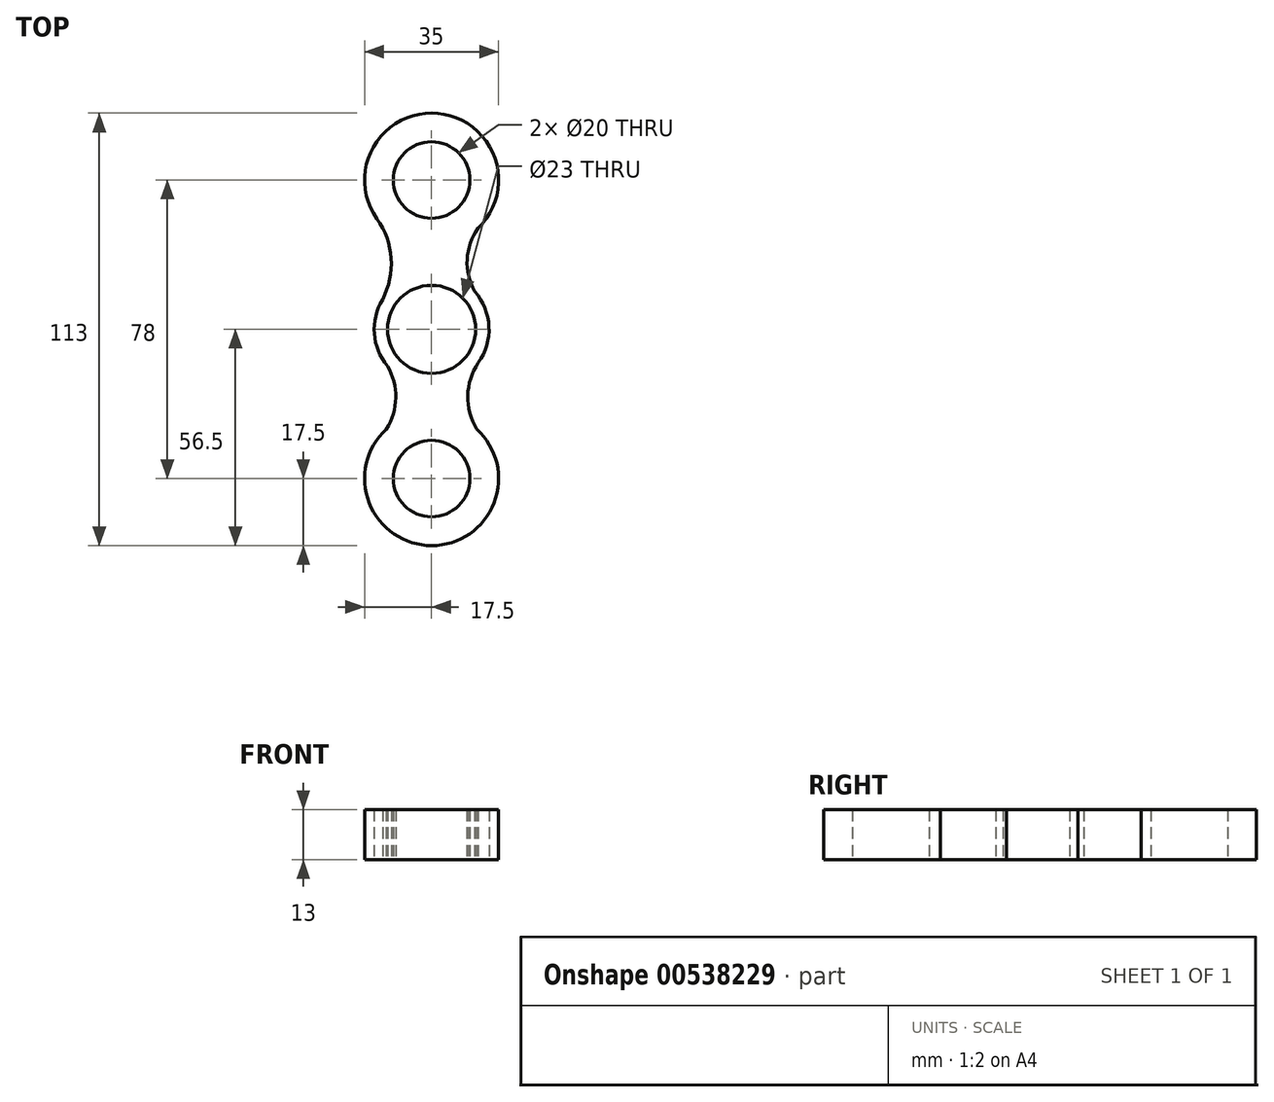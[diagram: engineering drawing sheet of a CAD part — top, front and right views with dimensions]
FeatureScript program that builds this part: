
annotation { "Feature Type Name" : "Feature", "Feature Type Description" : "" }
export const myFeature = defineFeature(function(context is Context, id is Id, definition is map)
    precondition{}
    {
        {
            var Q0;
            Q0=qCreatedBy(makeId("Top.planeOp"),FACE);
            var sketch = newSketch(context, id + "F0", { "sketchPlane" : qUnion([Q0])});
            skCircle(sketch, "E0", {"center": v(0, 0) * mm, "radius": 11.5 * mm});
            skCircle(sketch, "E1", {"center": v(0, 39) * mm, "radius": 10 * mm});
            skCircle(sketch, "E2", {"center": v(0, -39) * mm, "radius": 10 * mm});
            skCircle(sketch, "E3", {"center": v(0, 39) * mm, "radius": 17.5 * mm});
            skCircle(sketch, "E4", {"center": v(0, -39) * mm, "radius": 17.5 * mm});
            skCircle(sketch, "E5", {"center": v(0, 0) * mm, "radius": 15 * mm});
            skArc(sketch, "E6", {"start": v(-12.82, 7.8) * mm, "mid": v(-10.55, 18.52) * mm, "end": v(-14.25, 28.84) * mm});
            skArc(sketch, "E7", {"start": v(12.11, 26.37) * mm, "mid": v(9.28, 18.25) * mm, "end": v(11.28, 9.88) * mm});
            skArc(sketch, "E8", {"start": v(-11.84, -26.1) * mm, "mid": v(-9.37, -17.89) * mm, "end": v(-11.54, -9.58) * mm});
            skArc(sketch, "E9", {"start": v(12.18, -8.75) * mm, "mid": v(9.45, -17.35) * mm, "end": v(11.78, -26.06) * mm});
            skSolve(sketch);
        }
        {
            var Q0;
            Q0=makeQuery(id+"F0.imprint","IMPRINT",FACE,{"disambiguationData":[TD([[makeQuery(id+"F0.imprint","IMPRINT",EDGE,{"derivedFrom":sQuery(id+"F0.wireOp",EDGE,"E1")}),-1.0]])]});
            var Q1;
            Q1=makeQuery(id+"F0.imprint","IMPRINT",FACE,{"disambiguationData":[TD([[makeQuery(id+"F0.imprint","IMPRINT",EDGE,{"derivedFrom":sQuery(id+"F0.wireOp",EDGE,"E0")}),-1.0]])]});
            var Q2;
            Q2=qSketchRegion(id+"F0",true);
            var Q3;
            {var subQ0=sQuery(id+"F0.wireOp",EDGE,"E8");Q3=makeQuery(id+"F0.imprint","IMPRINT",FACE,{"disambiguationData":[TD([[makeQuery(id+"F0.imprint","IMPRINT",EDGE,{"derivedFrom":subQ0}),-1.0]])]});}
            var Q4;
            {var subQ0=sQuery(id+"F0.wireOp",EDGE,"E6");Q4=makeQuery(id+"F0.imprint","IMPRINT",FACE,{"disambiguationData":[TD([[makeQuery(id+"F0.imprint","IMPRINT",EDGE,{"derivedFrom":subQ0}),-1.0]])]});}
            extrude(context, id + "F1", {"entities" : qUnion([Q0, Q1, Q2, Q3, Q4]), "depth" : 13 * mm, "offsetDistance" : 25 * mm});
        }
    });
